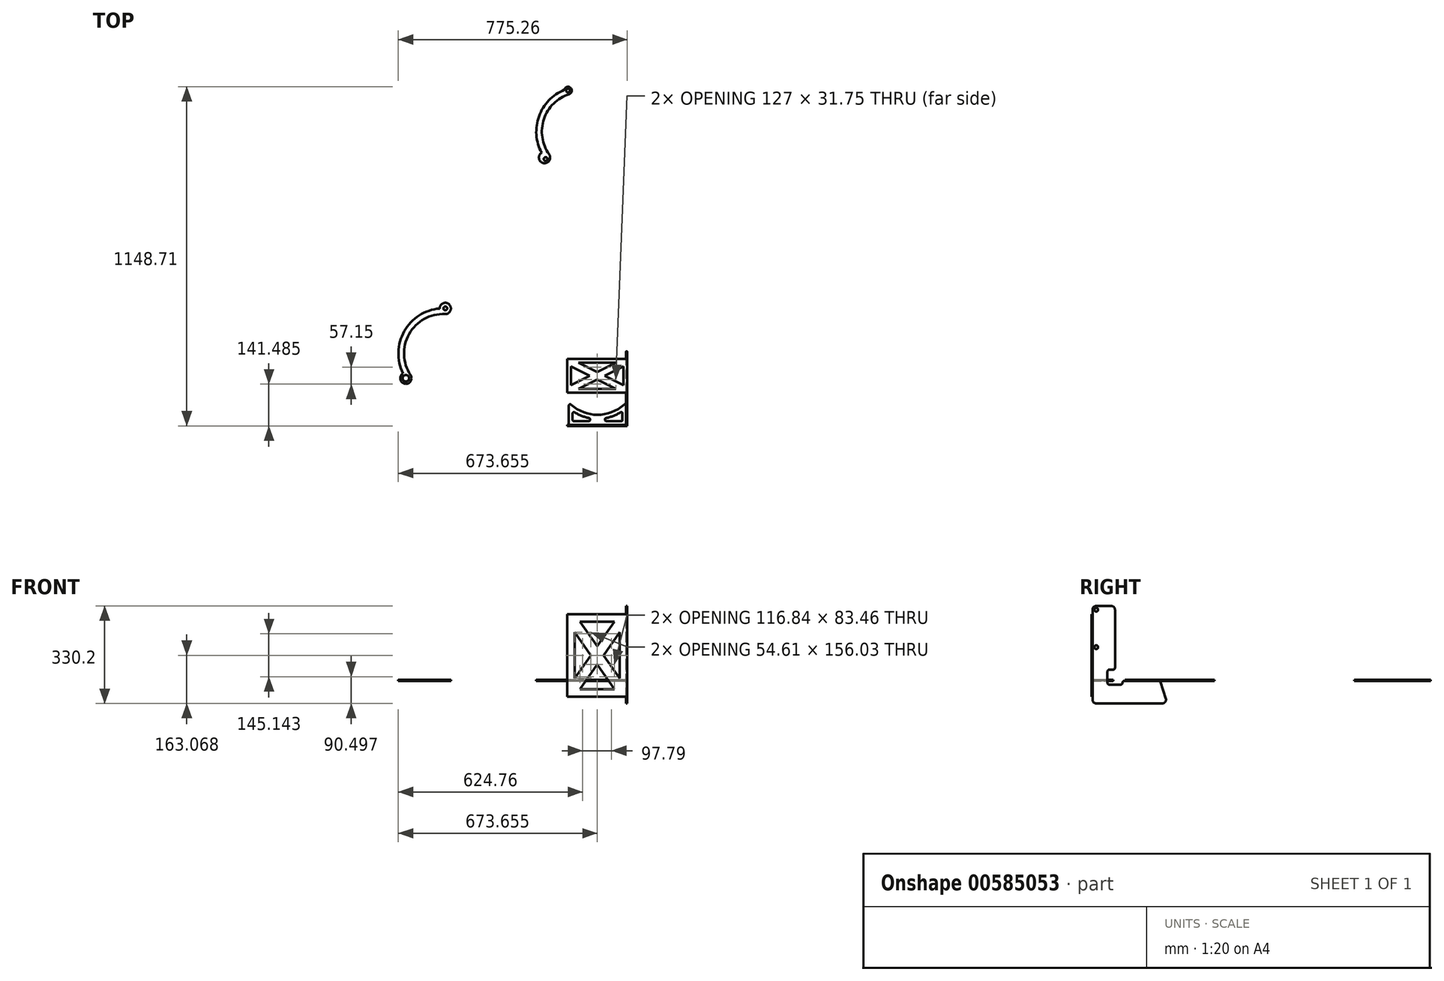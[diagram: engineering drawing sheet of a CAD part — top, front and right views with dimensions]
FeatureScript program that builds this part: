
annotation { "Feature Type Name" : "Feature", "Feature Type Description" : "" }
export const myFeature = defineFeature(function(context is Context, id is Id, definition is map)
    precondition{}
    {
        {
            var Q0;
            Q0=qCreatedBy(makeId("Right.planeOp"),FACE);
            var sketch = newSketch(context, id + "F0", { "sketchPlane" : qUnion([Q0])});
            skLineSegment(sketch, "E0", {"start": v(0, -12.7) * mm, "end": v(25.4, -12.7) * mm});
            skLineSegment(sketch, "E1", {"start": v(25.4, -12.7) * mm, "end": v(25.4, 0) * mm});
            skLineSegment(sketch, "E2", {"start": v(25.4, 0) * mm, "end": v(152.4, 0) * mm});
            skLineSegment(sketch, "E3", {"start": v(152.4, 0) * mm, "end": v(177.8, -76.2) * mm});
            skLineSegment(sketch, "E4", {"start": v(177.8, -76.2) * mm, "end": v(-76.2, -76.2) * mm});
            skLineSegment(sketch, "E5", {"start": v(-76.2, -76.2) * mm, "end": v(-76.2, 254) * mm});
            skLineSegment(sketch, "E6", {"start": v(-76.2, 254) * mm, "end": v(0, 254) * mm});
            skCircle(sketch, "E7", {"center": v(-63.5, 241.3) * mm, "radius": 6.35 * mm});
            skLineSegment(sketch, "E8.bottom", {"start": v(0, -12.7) * mm, "end": v(-25.4, -12.7) * mm});
            skLineSegment(sketch, "E8.top", {"start": v(0, 38.1) * mm, "end": v(-25.4, 38.1) * mm});
            skLineSegment(sketch, "E8.right", {"start": v(-25.4, -12.7) * mm, "end": v(-25.4, 38.1) * mm});
            skLineSegment(sketch, "E9", {"start": v(0, 38.1) * mm, "end": v(0, 254) * mm});
            skCircle(sketch, "E10.0.1.0", {"center": v(-63.5, 114.3) * mm, "radius": 6.35 * mm});
            skLineSegment(sketch, "E10.direction1", {"start": v(-63.5, 241.3) * mm, "end": v(-38.1, 241.3) * mm, "construction": true});
            skLineSegment(sketch, "E10.direction2", {"start": v(-63.5, 241.3) * mm, "end": v(-63.5, 114.3) * mm, "construction": true});
            skSolve(sketch);
        }
        {
            var Q0;
            Q0 = qSketchRegion(id + "F0", true);
            extrude(context, id + "F1", {"entities" : qUnion([Q0]), "depth" : 3.17 * mm, "offsetDistance" : 25.4 * mm});
        }
        {
            var Q0;
            Q0=makeQuery(id+"F1.opExtrude","SWEPT_EDGE",EDGE,{"disambiguationData":[OSD([sQuery(id+"F0.wireOp",EDGE,"E5"),sQuery(id+"F0.wireOp",EDGE,"E6")])]});
            var Q1;
            Q1=makeQuery(id+"F1.opExtrude","SWEPT_EDGE",EDGE,{"disambiguationData":[OSD([sQuery(id+"F0.wireOp",EDGE,"E6"),sQuery(id+"F0.wireOp",EDGE,"E9")])]});
            fillet(context, id + "F2", {"entities" : qUnion([Q0, Q1]), "tangentPropagation" : true, "radius" : 12.7 * mm, "defaultsChanged" : false, "vertexSettings" : [], "allowEdgeOverflow" : false});
        }
        {
            var Q0;
            Q0=makeQuery(id+"F1.opExtrude","SWEPT_EDGE",EDGE,{"disambiguationData":[OSD([sQuery(id+"F0.wireOp",EDGE,"E2"),sQuery(id+"F0.wireOp",EDGE,"E3")])]});
            var Q1;
            Q1=makeQuery(id+"F1.opExtrude","SWEPT_EDGE",EDGE,{"disambiguationData":[OSD([sQuery(id+"F0.wireOp",EDGE,"E1"),sQuery(id+"F0.wireOp",EDGE,"E2")])]});
            var Q2;
            Q2=makeQuery(id+"F1.opExtrude","SWEPT_EDGE",EDGE,{"disambiguationData":[OSD([sQuery(id+"F0.wireOp",EDGE,"E0"),sQuery(id+"F0.wireOp",EDGE,"E1")])]});
            var Q3;
            Q3=makeQuery(id+"F1.opExtrude","SWEPT_EDGE",EDGE,{"disambiguationData":[OSD([sQuery(id+"F0.wireOp",EDGE,"E0"),sQuery(id+"F0.wireOp",EDGE,"kD19vQGl-UHv5-4ZR1-Rwa7-xBA6NJApBEdt")])]});
            var Q4;
            Q4=makeQuery(id+"F1.opExtrude","SWEPT_EDGE",EDGE,{"disambiguationData":[OSD([sQuery(id+"F0.wireOp",EDGE,"E8.top"),sQuery(id+"F0.wireOp",EDGE,"E8.right")])]});
            var Q5;
            Q5=makeQuery(id+"F1.opExtrude","SWEPT_EDGE",EDGE,{"disambiguationData":[OSD([sQuery(id+"F0.wireOp",EDGE,"E8.top"),sQuery(id+"F0.wireOp",EDGE,"E9")])]});
            var Q6;
            Q6=makeQuery(id+"F1.opExtrude","SWEPT_EDGE",EDGE,{"disambiguationData":[OSD([sQuery(id+"F0.wireOp",EDGE,"E8.bottom"),sQuery(id+"F0.wireOp",EDGE,"E8.right")])]});
            fillet(context, id + "F3", {"entities" : qUnion([Q0, Q1, Q2, Q3, Q4, Q5, Q6]), "tangentPropagation" : true, "radius" : 6.35 * mm, "defaultsChanged" : false, "vertexSettings" : [], "allowEdgeOverflow" : false});
        }
        {
            var Q0;
            Q0=makeQuery(id+"F1.opExtrude","SWEPT_FACE",FACE,{"disambiguationData":[OSD([sQuery(id+"F0.wireOp",EDGE,"E2")])]});
            var sketch = newSketch(context, id + "F4", { "sketchPlane" : qUnion([Q0])});
            skLineSegment(sketch, "E11.bottom", {"start": v(3.17, 147.82) * mm, "end": v(-200.03, 147.82) * mm});
            skLineSegment(sketch, "E11.top", {"start": v(3.18, 33.52) * mm, "end": v(-200.02, 33.52) * mm});
            skLineSegment(sketch, "E11.left", {"start": v(3.18, 147.82) * mm, "end": v(3.18, 33.52) * mm});
            skLineSegment(sketch, "E11.right", {"start": v(-200.03, 147.82) * mm, "end": v(-200.02, 33.52) * mm});
            skLineSegment(sketch, "E12.bottom", {"start": v(-161.93, 135.13) * mm, "end": v(-34.92, 135.13) * mm});
            skLineSegment(sketch, "E12.top", {"start": v(-161.92, 46.23) * mm, "end": v(-34.92, 46.23) * mm});
            skLineSegment(sketch, "E12.left", {"start": v(-187.32, 122.43) * mm, "end": v(-187.32, 58.93) * mm});
            skLineSegment(sketch, "E12.right", {"start": v(-9.52, 122.43) * mm, "end": v(-9.52, 58.93) * mm});
            skLineSegment(sketch, "E13", {"start": v(-161.93, 135.13) * mm, "end": v(-98.42, 103.38) * mm});
            skLineSegment(sketch, "E14", {"start": v(-187.33, 122.43) * mm, "end": v(-123.83, 90.68) * mm});
            skLineSegment(sketch, "E15", {"start": v(-34.92, 135.13) * mm, "end": v(-98.42, 103.38) * mm});
            skLineSegment(sketch, "E16", {"start": v(-9.52, 122.43) * mm, "end": v(-73.02, 90.68) * mm});
            skLineSegment(sketch, "E17", {"start": v(-187.32, 46.23) * mm, "end": v(-9.52, 135.13) * mm, "construction": true});
            skPoint(sketch, "E18.orphan", {"position": v(-9.52, 46.23) * mm});
            skLineSegment(sketch, "E19.trimOffspring", {"start": v(-123.83, 90.68) * mm, "end": v(-187.32, 58.93) * mm});
            skLineSegment(sketch, "E20.trimOffspring", {"start": v(-98.42, 77.98) * mm, "end": v(-34.92, 46.23) * mm});
            skLineSegment(sketch, "E21.trimOffspring", {"start": v(-73.02, 90.68) * mm, "end": v(-9.52, 58.93) * mm});
            skLineSegment(sketch, "E22.trimOffspring", {"start": v(-98.42, 77.98) * mm, "end": v(-161.92, 46.23) * mm});
            skSolve(sketch);
        }
        {
            var Q0;
            Q0 = qSketchRegion(id + "F4", true);
            extrude(context, id + "F5", {"entities" : qUnion([Q0]), "depth" : 3.17 * mm, "offsetDistance" : 25.4 * mm});
        }
        {
            var Q0;
            Q0=makeQuery(id+"F1.opExtrude","SWEPT_FACE",FACE,{"disambiguationData":[OSD([sQuery(id+"F0.wireOp",EDGE,"E5")])]});
            var sketch = newSketch(context, id + "F6", { "sketchPlane" : qUnion([Q0])});
            skLineSegment(sketch, "E23.bottom", {"start": v(3.17, 241.3) * mm, "end": v(-200.03, 241.3) * mm});
            skLineSegment(sketch, "E23.top", {"start": v(3.18, -38.1) * mm, "end": v(-200.02, -38.1) * mm});
            skLineSegment(sketch, "E23.left", {"start": v(3.18, 241.3) * mm, "end": v(3.18, -38.1) * mm});
            skLineSegment(sketch, "E23.right", {"start": v(-200.03, 241.3) * mm, "end": v(-200.02, -38.1) * mm});
            skPoint(sketch, "E24.middle.positionSnap1", {"position": v(-98.43, 241.3) * mm});
            skPoint(sketch, "E24.centerSnap1", {"position": v(-98.43, 241.3) * mm});
            skLineSegment(sketch, "E25", {"start": v(-98.43, 228.6) * mm, "end": v(-98.43, 241.3) * mm, "construction": true});
            skLineSegment(sketch, "E26.0", {"start": v(-40, -12.7) * mm, "end": v(-156.84, -12.7) * mm});
            skLineSegment(sketch, "E27.0", {"start": v(-22.22, 179.61) * mm, "end": v(-22.22, 23.59) * mm});
            skLineSegment(sketch, "E28", {"start": v(-156.84, 215.9) * mm, "end": v(-98.42, 132.44) * mm});
            skLineSegment(sketch, "E29", {"start": v(-40, -12.7) * mm, "end": v(-98.42, 70.76) * mm});
            skLineSegment(sketch, "E30", {"start": v(-40, 215.9) * mm, "end": v(-98.42, 132.44) * mm});
            skLineSegment(sketch, "E31", {"start": v(-156.84, -12.7) * mm, "end": v(-98.42, 70.76) * mm});
            skLineSegment(sketch, "E32.trimOffspring", {"start": v(-174.62, 179.61) * mm, "end": v(-174.62, 23.59) * mm});
            skLineSegment(sketch, "E33.trimOffspring", {"start": v(-40, 215.9) * mm, "end": v(-156.84, 215.9) * mm});
            skLineSegment(sketch, "E34.trimOffspring", {"start": v(-120.01, 101.6) * mm, "end": v(-174.63, 23.59) * mm});
            skLineSegment(sketch, "E35.trimOffspring", {"start": v(-76.83, 101.6) * mm, "end": v(-22.22, 23.59) * mm});
            skLineSegment(sketch, "E36.trimOffspring", {"start": v(-76.83, 101.6) * mm, "end": v(-22.22, 179.61) * mm});
            skLineSegment(sketch, "E37.trimOffspring", {"start": v(-120.01, 101.6) * mm, "end": v(-174.62, 179.61) * mm});
            skSolve(sketch);
        }
        {
            var Q0;
            Q0 = qSketchRegion(id + "F6", true);
            extrude(context, id + "F7", {"entities" : qUnion([Q0]), "depth" : 3.17 * mm, "offsetDistance" : 25.4 * mm});
        }
        {
            var Q0;
            Q0=makeQuery(id+"F7.opExtrude","SWEPT_BODY",BODY,{"disambiguationData":[OSD([sQuery(id+"F6.wireOp",EDGE,"E23.bottom"),sQuery(id+"F6.wireOp",EDGE,"E23.top"),sQuery(id+"F6.wireOp",EDGE,"E23.left"),sQuery(id+"F6.wireOp",EDGE,"E23.right"),sQuery(id+"F6.wireOp",EDGE,"SXseGbRr-w6uI-T8Wt-dOCc-sjlZz6noJ7lP"),sQuery(id+"F6.wireOp",EDGE,"mp5M7fCn-CwH5-Elwd-d4ZR-C4dLEL63u4mO"),sQuery(id+"F6.wireOp",EDGE,"d7cd7813-de51-424e-9822-0e871deb18e70.MirrorCS"),sQuery(id+"F6.wireOp",EDGE,"d7cd7813-de51-424e-9822-0e871deb18e71.MirrorCS"),sQuery(id+"F6.wireOp",EDGE,"kcJgZt31-MEAo-3p8t-nxGZ-3nQ9wFXIwk5l"),sQuery(id+"F6.wireOp",EDGE,"rZmhDnz9-0NTC-tZZx-6KIt-nNh4iq2fBSdj"),sQuery(id+"F6.wireOp",EDGE,"QhxO05B9-O90v-4jpr-uqlf-Rbg1w0xvRdPR"),sQuery(id+"F6.wireOp",EDGE,"ILQycdQO-LiSL-a0c1-bmhv-3g5EyDnMlrBU"),sQuery(id+"F6.wireOp",EDGE,"1ed7c068-8182-4526-95cd-e7e32c386e41.trimOffspring"),sQuery(id+"F6.wireOp",EDGE,"015a5685-02d7-4efb-8cc3-2f9e11e8c8d3.trimOffspring"),sQuery(id+"F6.wireOp",EDGE,"0fd6fe91-38cf-4b8c-aeca-cf303f3f98a1.trimOffspring"),sQuery(id+"F6.wireOp",EDGE,"247e1c8c-b361-4233-8e1d-8844c5410c9f.trimOffspring")])]});
            transform(context, id + "F8", {"entities" : qUnion([Q0]), "transformType" : TransformType.TRANSLATION_3D, "dx" : 0 * mm, "dy" : 0 * mm, "dz" : -14.73 * mm, "makeCopy" : false});
        }
        {
            var Q0;
            Q0=qCreatedBy(makeId("Top.planeOp"),FACE);
            var sketch = newSketch(context, id + "F9", { "sketchPlane" : qUnion([Q0])});
            skLineSegment(sketch, "E38", {"start": v(0, 0) * mm, "end": v(0, 88.2) * mm, "construction": true});
            skLineSegment(sketch, "E39", {"start": v(0, 88.2) * mm, "end": v(-100.01, 88.2) * mm, "construction": true});
            skLineSegment(sketch, "E40", {"start": v(-194.31, 0) * mm, "end": v(-194.31, -76.2) * mm});
            skLineSegment(sketch, "E41", {"start": v(-194.31, -76.2) * mm, "end": v(0, -76.2) * mm});
            skLineSegment(sketch, "E42", {"start": v(0, -76.2) * mm, "end": v(0, 0) * mm});
            skArc(sketch, "E43", {"start": v(0, 0) * mm, "mid": v(-97.16, -42) * mm, "end": v(-194.31, 0) * mm});
            skLineSegment(sketch, "E44.0", {"start": v(-12.7, -63.5) * mm, "end": v(-12.7, -28.87) * mm});
            skLineSegment(sketch, "E45.0", {"start": v(-181.61, -63.5) * mm, "end": v(-122.55, -63.5) * mm});
            skLineSegment(sketch, "E46.left", {"start": v(-122.55, -53.54) * mm, "end": v(-122.55, -63.5) * mm});
            skLineSegment(sketch, "E46.right", {"start": v(-71.75, -53.54) * mm, "end": v(-71.75, -63.5) * mm});
            skLineSegment(sketch, "E47.trimOffspring", {"start": v(-181.61, -28.87) * mm, "end": v(-181.61, -63.5) * mm});
            skArc(sketch, "E48.trimOffspring", {"start": v(-12.7, -28.87) * mm, "mid": v(-40.86, -44.48) * mm, "end": v(-71.75, -53.54) * mm});
            skArc(sketch, "E49.trimOffspring", {"start": v(-122.55, -53.54) * mm, "mid": v(-153.45, -44.48) * mm, "end": v(-181.61, -28.87) * mm});
            skLineSegment(sketch, "E50.trimOffspring", {"start": v(-71.75, -63.5) * mm, "end": v(-12.7, -63.5) * mm});
            skSolve(sketch);
        }
        {
            var Q0;
            Q0 = qSketchRegion(id + "F9", true);
            extrude(context, id + "F10", {"entities" : qUnion([Q0]), "depth" : 3.17 * mm, "offsetDistance" : 25.4 * mm});
        }
        {
            var Q0;
            Q0=makeQuery(id+"F10.opExtrude","SWEPT_EDGE",EDGE,{"disambiguationData":[OSD([sQuery(id+"F9.wireOp",EDGE,"E45.0"),sQuery(id+"F9.wireOp",EDGE,"E46.left")])]});
            var Q1;
            Q1=makeQuery(id+"F10.opExtrude","SWEPT_EDGE",EDGE,{"disambiguationData":[OSD([sQuery(id+"F9.wireOp",EDGE,"E46.left"),sQuery(id+"F9.wireOp",EDGE,"E49.trimOffspring")])]});
            var Q2;
            Q2=makeQuery(id+"F10.opExtrude","SWEPT_EDGE",EDGE,{"disambiguationData":[OSD([sQuery(id+"F9.wireOp",EDGE,"E45.0"),sQuery(id+"F9.wireOp",EDGE,"E47.trimOffspring")])]});
            var Q3;
            Q3=makeQuery(id+"F10.opExtrude","SWEPT_EDGE",EDGE,{"disambiguationData":[OSD([sQuery(id+"F9.wireOp",EDGE,"E47.trimOffspring"),sQuery(id+"F9.wireOp",EDGE,"E49.trimOffspring")])]});
            var Q4;
            Q4=makeQuery(id+"F10.opExtrude","SWEPT_EDGE",EDGE,{"disambiguationData":[OSD([sQuery(id+"F9.wireOp",EDGE,"E44.0"),sQuery(id+"F9.wireOp",EDGE,"E50.trimOffspring")])]});
            var Q5;
            Q5=makeQuery(id+"F10.opExtrude","SWEPT_EDGE",EDGE,{"disambiguationData":[OSD([sQuery(id+"F9.wireOp",EDGE,"E46.right"),sQuery(id+"F9.wireOp",EDGE,"E50.trimOffspring")])]});
            var Q6;
            Q6=makeQuery(id+"F10.opExtrude","SWEPT_EDGE",EDGE,{"disambiguationData":[OSD([sQuery(id+"F9.wireOp",EDGE,"E46.right"),sQuery(id+"F9.wireOp",EDGE,"E48.trimOffspring")])]});
            var Q7;
            Q7=makeQuery(id+"F10.opExtrude","SWEPT_EDGE",EDGE,{"disambiguationData":[OSD([sQuery(id+"F9.wireOp",EDGE,"E44.0"),sQuery(id+"F9.wireOp",EDGE,"E48.trimOffspring")])]});
            var Q8;
            Q8=makeQuery(id+"F10.opExtrude","SWEPT_EDGE",EDGE,{"disambiguationData":[OSD([sQuery(id+"F9.wireOp",EDGE,"E40"),sQuery(id+"F9.wireOp",EDGE,"E43")])]});
            var Q9;
            Q9=makeQuery(id+"F10.opExtrude","SWEPT_EDGE",EDGE,{"disambiguationData":[OSD([sQuery(id+"F9.wireOp",EDGE,"E42"),sQuery(id+"F9.wireOp",EDGE,"E43")])]});
            fillet(context, id + "F11", {"entities" : qUnion([Q0, Q1, Q2, Q3, Q4, Q5, Q6, Q7, Q8, Q9]), "tangentPropagation" : true, "radius" : 4.44 * mm, "defaultsChanged" : true, "vertexSettings" : [], "allowEdgeOverflow" : false});
        }
        {
            var Q0;
            Q0=makeQuery(id+"F1.opExtrude","SWEPT_EDGE",EDGE,{"disambiguationData":[OSD([sQuery(id+"F0.wireOp",EDGE,"E4"),sQuery(id+"F0.wireOp",EDGE,"E5")])]});
            var Q1;
            Q1=makeQuery(id+"F1.opExtrude","SWEPT_EDGE",EDGE,{"disambiguationData":[OSD([sQuery(id+"F0.wireOp",EDGE,"E3"),sQuery(id+"F0.wireOp",EDGE,"E4")])]});
            fillet(context, id + "F12", {"entities" : qUnion([Q0, Q1]), "tangentPropagation" : true, "radius" : 12.7 * mm, "defaultsChanged" : false, "vertexSettings" : [], "allowEdgeOverflow" : false});
        }
        {
            var Q0;
            Q0=qCreatedBy(makeId("Top.planeOp"),FACE);
            var sketch = newSketch(context, id + "F13", { "sketchPlane" : qUnion([Q0])});
            skArc(sketch, "E51", {"start": v(-756.2, 98.48) * mm, "mid": v(-751.06, 63.44) * mm, "end": v(-730.81, 92.5) * mm});
            skCircle(sketch, "E52", {"center": v(-746.7, 81.98) * mm, "radius": 10.8 * mm});
            skCircle(sketch, "E53", {"center": v(-613.15, 318.44) * mm, "radius": 6.35 * mm});
            skArc(sketch, "E54.trimOffspring", {"start": v(-632.2, 318.07) * mm, "mid": v(-752.39, 241.13) * mm, "end": v(-756.2, 98.48) * mm});
            skArc(sketch, "E55", {"start": v(-613.97, 299.41) * mm, "mid": v(-599.52, 331.76) * mm, "end": v(-632.2, 318.07) * mm});
            skArc(sketch, "E56", {"start": v(-730.81, 92.5) * mm, "mid": v(-735.8, 231.76) * mm, "end": v(-613.97, 299.41) * mm});
            skSolve(sketch);
        }
        {
            var Q0;
            Q0 = qSketchRegion(id + "F13", true);
            extrude(context, id + "F14", {"entities" : qUnion([Q0]), "depth" : 3.17 * mm, "offsetDistance" : 25.4 * mm});
        }
        {
            var Q0;
            Q0=qCreatedBy(makeId("Top.planeOp"),FACE);
            var sketch = newSketch(context, id + "F15", { "sketchPlane" : qUnion([Q0])});
            skArc(sketch, "E57", {"start": v(-193.2, 1044.53) * mm, "mid": v(-278.9, 959.8) * mm, "end": v(-261.27, 840.58) * mm});
            skLineSegment(sketch, "E58.bottom", {"start": v(-31.75, 1010.7) * mm, "end": v(-273.05, 1010.7) * mm, "construction": true});
            skLineSegment(sketch, "E58.top", {"start": v(-31.75, 824.47) * mm, "end": v(-273.05, 824.47) * mm, "construction": true});
            skLineSegment(sketch, "E58.left", {"start": v(-31.75, 824.47) * mm, "end": v(-31.75, 1010.7) * mm, "construction": true});
            skLineSegment(sketch, "E58.right", {"start": v(-273.05, 824.47) * mm, "end": v(-273.05, 1010.7) * mm, "construction": true});
            skLineSegment(sketch, "E59", {"start": v(-152.4, 917.58) * mm, "end": v(-152.4, 1069.98) * mm, "construction": true});
            skArc(sketch, "E60", {"start": v(-193.2, 1044.53) * mm, "mid": v(-188.74, 1066.2) * mm, "end": v(-209.6, 1058.84) * mm});
            skCircle(sketch, "E61", {"center": v(-197.1, 1056.63) * mm, "radius": 6.35 * mm});
            skArc(sketch, "E62.trimOffspring", {"start": v(-209.6, 1058.84) * mm, "mid": v(-295.68, 969.52) * mm, "end": v(-286.83, 845.79) * mm});
            skArc(sketch, "E63", {"start": v(-258.36, 836.61) * mm, "mid": v(-44.97, 996.58) * mm, "end": v(-261.27, 840.58) * mm, "construction": true});
            skArc(sketch, "E64", {"start": v(-283.73, 840.26) * mm, "mid": v(-19.5, 992.15) * mm, "end": v(-286.83, 845.79) * mm, "construction": true});
            skCircle(sketch, "E65", {"center": v(-273.05, 824.47) * mm, "radius": 6.35 * mm});
            skLineSegment(sketch, "E66", {"start": v(-273.05, 824.47) * mm, "end": v(-258.36, 836.61) * mm, "construction": true});
            skLineSegment(sketch, "E67", {"start": v(-152.4, 917.58) * mm, "end": v(-152.4, 784.23) * mm, "construction": true});
            skArc(sketch, "E68", {"start": v(-286.83, 845.79) * mm, "mid": v(-280.63, 810.91) * mm, "end": v(-261.27, 840.58) * mm});
            skSolve(sketch);
        }
        {
            var Q0;
            Q0 = qSketchRegion(id + "F15", true);
            extrude(context, id + "F16", {"entities" : qUnion([Q0]), "depth" : 3.17 * mm, "offsetDistance" : 25.4 * mm});
        }
    });
